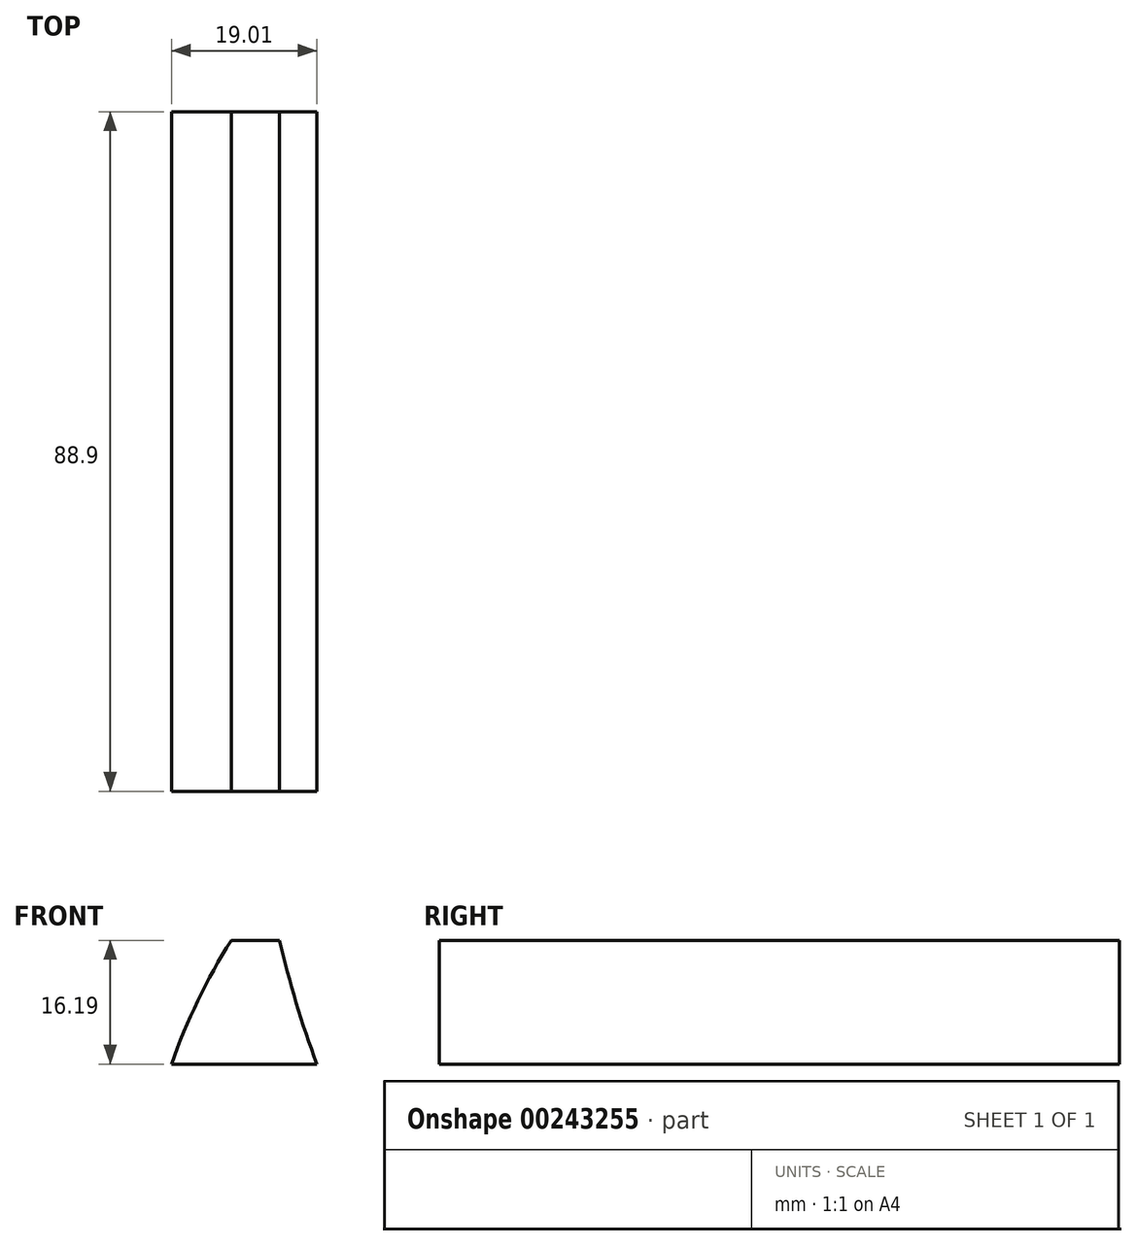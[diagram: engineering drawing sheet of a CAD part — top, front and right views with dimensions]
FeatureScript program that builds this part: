
annotation { "Feature Type Name" : "Feature", "Feature Type Description" : "" }
export const myFeature = defineFeature(function(context is Context, id is Id, definition is map)
    precondition{}
    {
        {
            var Q0;
            Q0=qCreatedBy(makeId("Front.planeOp"),FACE);
            var sketch = newSketch(context, id + "F0", { "sketchPlane" : qUnion([Q0])});
            skLineSegment(sketch, "E0", {"start": v(30.72, 11) * mm, "end": v(-74.06, 11) * mm});
            skCircle(sketch, "E1", {"center": v(68.8, 39.29) * mm, "radius": 127 * mm});
            skCircle(sketch, "E2", {"center": v(10.08, -33.46) * mm, "radius": 84.14 * mm});
            skLineSegment(sketch, "E3", {"start": v(-72.6, -17.9) * mm, "end": v(-44.6, -17.9) * mm});
            skLineSegment(sketch, "E4", {"start": v(-69.17, -5.2) * mm, "end": v(-50.16, -5.2) * mm});
            skSolve(sketch);
        }
        {
            var Q0;
            {var subQ5=sQuery(id+"F0.wireOp",EDGE,"E4");Q0=makeQuery(id+"F0.imprint","IMPRINT",FACE,{"disambiguationData":[TD([[makeQuery(id+"F0.imprint","IMPRINT",EDGE,{"derivedFrom":subQ5}),1.0]])]});}
            extrude(context, id + "F1", {"entities" : qUnion([Q0]), "depth" : 88.9 * mm});
        }
    });
